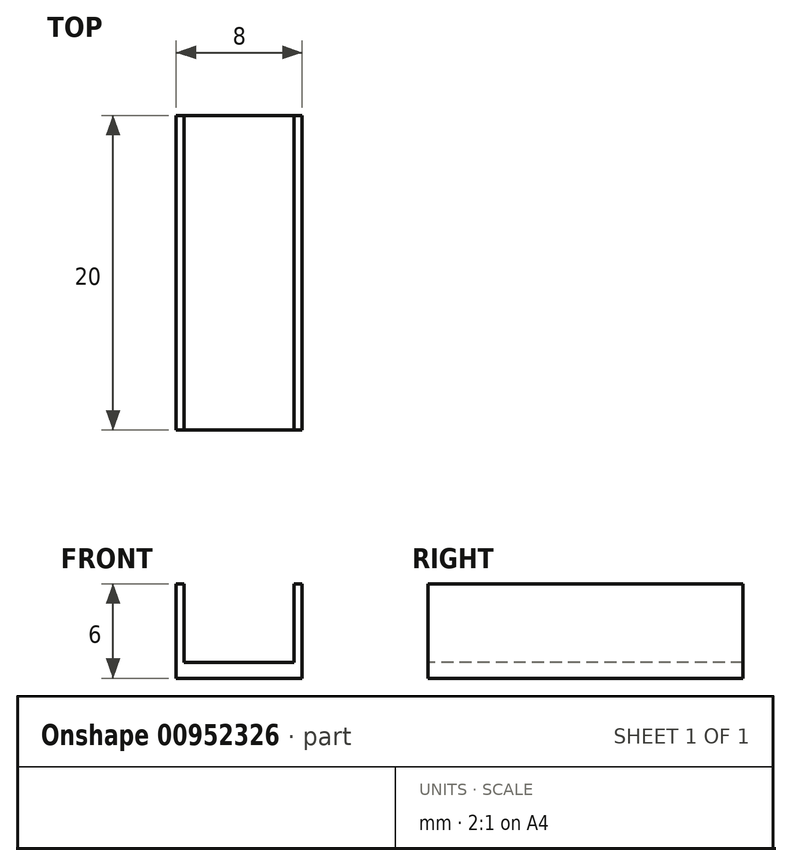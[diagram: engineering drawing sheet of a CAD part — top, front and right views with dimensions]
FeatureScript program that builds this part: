
annotation { "Feature Type Name" : "Feature", "Feature Type Description" : "" }
export const myFeature = defineFeature(function(context is Context, id is Id, definition is map)
    precondition{}
    {
        {
            var Q0;
            Q0=qCreatedBy(makeId("Front.planeOp"),FACE);
            var sketch = newSketch(context, id + "F0", { "sketchPlane" : qUnion([Q0])});
            skLineSegment(sketch, "E0.bottom", {"start": v(0, 6) * mm, "end": v(0.5, 6) * mm});
            skLineSegment(sketch, "E0.top", {"start": v(0, 0) * mm, "end": v(0.5, 0) * mm});
            skLineSegment(sketch, "E0.left", {"start": v(0, 6) * mm, "end": v(0, 0) * mm});
            skLineSegment(sketch, "E0.right", {"start": v(0.5, 6) * mm, "end": v(0.5, 1) * mm});
            skLineSegment(sketch, "E1.bottom", {"start": v(0.5, 0) * mm, "end": v(7.5, 0) * mm});
            skLineSegment(sketch, "E1.top", {"start": v(0.5, 1) * mm, "end": v(7.5, 1) * mm});
            skLineSegment(sketch, "E2.bottom", {"start": v(7.5, 0) * mm, "end": v(8, 0) * mm});
            skLineSegment(sketch, "E2.top", {"start": v(7.5, 6) * mm, "end": v(8, 6) * mm});
            skLineSegment(sketch, "E2.left", {"start": v(7.5, 1) * mm, "end": v(7.5, 6) * mm});
            skLineSegment(sketch, "E2.right", {"start": v(8, 0) * mm, "end": v(8, 6) * mm});
            skSolve(sketch);
        }
        {
            var Q0;
            Q0 = qSketchRegion(id + "F0", true);
            extrude(context, id + "F1", {"entities" : qUnion([Q0]), "oppositeDirection" : true, "depth" : 20 * mm, "offsetDistance" : 25 * mm});
        }
    });
